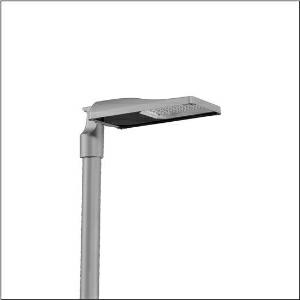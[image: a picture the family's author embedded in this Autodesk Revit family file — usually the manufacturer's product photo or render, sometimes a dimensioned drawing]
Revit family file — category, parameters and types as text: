
# Revit family: streetlight_sl_31_mini___st1_0a_5xh2d3ab08ga_301b
name_source: partatom
category: Lighting Fixtures
units: mm (PartAtom-declared; Revit-internal decimal feet)

## family parameters
Cut with Voids When Loaded = No
Host = Face
Light Source = No
Part Type = Normal
Room Calculation Point = No
Round Connector Dimension = Use Diameter
Shared = No

## types (1)
- --- (1 x LED, 5710 lm, 37.3 W, 3000K)
    Apparent Load = 37 VA
    CIE Flux Codes = 37 72 97 100 100
    Color Rendering = 70
    Color Temperature = 3000K
    Default Elevation = 1800 mm
    Description = Streetlight SL 31 mini Easy LST mast luminaire for post-top, side-entry; light control with lens of PMMA; light distribution: ST1.0a, direct asymmetric distribution, for standard-compliant lighting for roads and squares; LED: luminous flux: 5.710lm, light colour: 730, colour temperature: 3000K; luminous efficacy: 153,1lm/W; control: pre-setting: linear dimming characteristic, flexible luminous flux parameterisation, time-dependent luminous flux control, constant luminous flux control, power reduction, intelligent temperature release in ECG and LED module, overheat protection; luminaire housing, of diecast aluminium, Siteco® metallic grey (DB 702S), corrosivity category C5 high according to DIN EN ISO 12944; cover of toughened safety glass, transparent, mast flange of diecast aluminium, Siteco® metallic grey (DB 702S), spigot size: 76/60mm, mast flange included unmounted; with cable H07RN-F 3x 1.5mm², cable length: 6,5m, connection cable pre-assembled; mains connection: 220..240V, AC, 50/60Hz; power consumption (at start of service life): 37,3W / (at end of service life): 38,7W / (with reduced operation 50%): 17,5W; protection rating (complete): IP66; insulation class (complete): insulation class II (safety insulation); impact resistance: IK09; certification: CE, ENEC, ENEC+, VDE, UKCA; permissible operating ambient temperature for outdoor applications: -40..+50°C; packaging unit: 1 piece

Light Distribution: ST1.0a
    Height = 76 mm
    Lamp = 1 x LED
    Lamp Light Flux = 5710 lm
    Lamp Power = 37.3 W
    Lamp count = 1
    Length = 547 mm
    Luminous efficacy = 153 lm/W
    Manufacturer = Siteco
    ModVariant = No
    Model = 5XH2D3AB08GA
    Number of Poles = 1
    OnlyDefault = Yes
    Power Factor = 1
    Product Name = Streetlight SL 31 mini | ST1.0a
    Product group = mast luminaire | pylon top
    ProductGroupID = 6100
    Protection Class = Protection class II
    Protection Degree = IP 66
    RLX_Detail_Level = 1
    RLX_Emergency_Light_Flux = 0 lm
    RLX_Emergency_Type = 0
    RLX_Emergency_Type_DB = No
    RlxData = <blob elided: 39433 chars, md5=d799530c>
    Socket = socket
    Standby Power = 0 W
    System Light Flux = 5710 lm
    System Power = 37 W
    Type Comments = factory setting: luminous flux: 100 % | dim-lin: 254 | 386 mA
    Type Image = l_1300326.jpg
    URL = http://relux.com
    VarID = @adj_051986
    Voltage = 0 V
    Weight = 0.00 kg
    Width = 265 mm

## geometry (parser evidence)
native form markers: Blend x4, Sweep x10
no freeform markers — native parametric forms only
